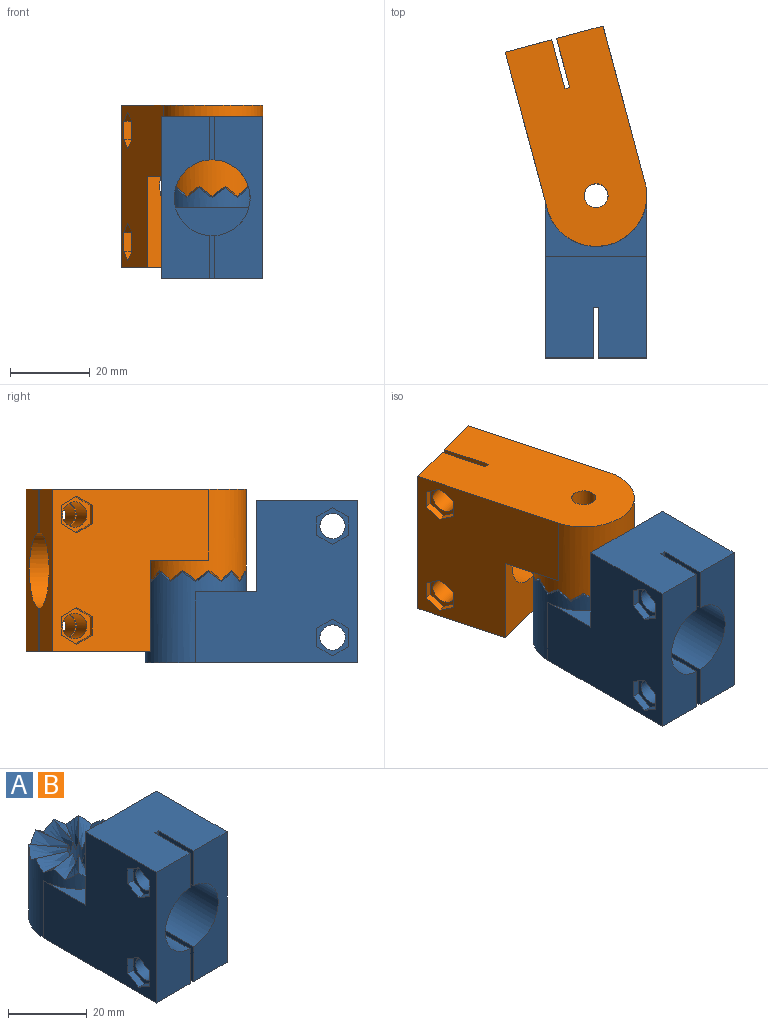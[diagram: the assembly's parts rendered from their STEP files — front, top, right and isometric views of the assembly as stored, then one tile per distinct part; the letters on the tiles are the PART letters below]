
ASSEMBLY  parts=2 mates=1
PART A: 62 faces, bbox 25.4x53.3x40.6 mm
  f0: plane 40.64x40.64mm, normal (-1,0,0), area 1192.4mm2, adj f3,f4,f5,f30,f31,f33,f49,f50
  f1: cylinder r=3.17mm len=10.07mm, axis (1,0,0), area 200.8mm2, adj f42,f55
  f2: cylinder r=3.17mm len=10.07mm, axis (1,0,0), area 200.8mm2, adj f39,f48
  f3: plane 40.64x12.07mm, normal (0,-1,0), area 359.9mm2, adj f0,f4,f31,f36,f39,f42
  f4: plane 25.4x25.4mm, normal (0,0,1), area 629mm2, adj f0,f3,f5,f32,f34,f41,f42,f43
  f5: plane 25.4x22.86mm, normal (0,1,0), area 390.3mm2, adj f0,f4,f32,f33,f36
  f6: bspline ~10.5x5.67mm, area 31.8mm2, adj f7,f29,f30,f35
  f7: bspline ~9.14x8.03mm, area 31.8mm2, adj f6,f8,f30,f35
  f8: bspline ~9.14x8.03mm, area 31.8mm2, adj f7,f9,f30,f35
  f9: bspline ~10.5x5.67mm, area 31.8mm2, adj f8,f10,f30,f35
  f10: bspline ~10.16x3.81mm, area 31.8mm2, adj f9,f11,f30,f35
  f11: bspline ~10.16x3.81mm, area 31.8mm2, adj f10,f12,f30,f35
  f12: bspline ~10.5x5.67mm, area 31.8mm2, adj f11,f13,f30,f35
  f13: bspline ~9.14x8.03mm, area 31.8mm2, adj f12,f14,f30,f35
  f14: bspline ~9.14x8.03mm, area 31.8mm2, adj f13,f15,f30,f35
  f15: bspline ~10.5x5.67mm, area 31.8mm2, adj f14,f16,f30,f35
  f16: bspline ~10.16x3.81mm, area 31.8mm2, adj f15,f17,f30,f35
  f17: bspline ~10.16x3.81mm, area 31.8mm2, adj f16,f18,f30,f35
  f18: bspline ~10.5x5.67mm, area 31.8mm2, adj f17,f19,f30,f35
  f19: bspline ~9.14x8.03mm, area 31.8mm2, adj f18,f20,f30,f35
  f20: bspline ~9.14x8.03mm, area 31.8mm2, adj f19,f21,f30,f35
  f21: bspline ~10.5x5.67mm, area 31.8mm2, adj f20,f22,f30,f35
  f22: bspline ~10.16x3.81mm, area 31.8mm2, adj f21,f23,f30,f35
  f23: bspline ~10.16x3.81mm, area 31.8mm2, adj f22,f24,f30,f35
  f24: bspline ~10.5x5.67mm, area 31.8mm2, adj f23,f25,f30,f35
  f25: bspline ~9.14x8.03mm, area 31.8mm2, adj f24,f26,f30,f35
  f26: bspline ~9.14x8.03mm, area 31.8mm2, adj f25,f27,f30,f35
  f27: bspline ~10.5x5.67mm, area 31.8mm2, adj f26,f28,f30,f35
  f28: bspline ~10.16x3.81mm, area 31.8mm2, adj f27,f29,f30,f35
  f29: bspline ~10.16x3.81mm, area 31.8mm2, adj f6,f28,f30,f35
  f30: cylinder r=12.7mm len=25.4mm, axis (0,0,-1), area 1011.1mm2, adj f0,f6,f7,f8,f9,f10,f11,f12
  f31: plane 53.34x25.4mm, normal (0,0,-1), area 1241.2mm2, adj f0,f3,f30,f32,f34,f35,f38,f39
  f32: plane 40.64x40.64mm, normal (1,0,0), area 1098mm2, adj f4,f5,f30,f31,f33,f34,f46,f47
  f33: plane 25.4x15.24mm, normal (0,0,1), area 133.7mm2, adj f0,f5,f30,f32,f37
  f34: plane 40.64x12.07mm, normal (0,-1,0), area 359.9mm2, adj f4,f31,f32,f36,f40,f41
  f35: cylinder r=3mm len=21.63mm, axis (0,0,-1), area 384mm2, adj f6,f7,f8,f9,f10,f11,f12,f13
  f36: cylinder r=9.53mm len=25.4mm, axis (0,-1,0), area 1487.8mm2, adj f3,f5,f34,f37,f38,f39,f40,f41
  f37: plane 18.36x6.99mm, normal (0,-1,0), area 94.7mm2, adj f33,f36
  f38: plane 10.82x1.27mm, normal (0,-1,0), area 13.7mm2, adj f31,f36,f39,f40
  f39: plane 12.7x10.82mm, normal (1,0,0), area 105.7mm2, adj f2,f3,f31,f36,f38
  f40: plane 12.7x10.82mm, normal (-1,0,0), area 105.7mm2, adj f31,f34,f36,f38,f45
  f41: plane 12.7x10.82mm, normal (-1,0,0), area 105.7mm2, adj f4,f34,f36,f43,f44
  f42: plane 12.7x10.82mm, normal (1,0,0), area 105.7mm2, adj f1,f3,f4,f36,f43
  f43: plane 10.82x1.27mm, normal (0,-1,0), area 13.7mm2, adj f4,f36,f41,f42
  f44: cylinder r=3.17mm len=9.53mm, axis (1,0,0), area 190mm2, adj f41,f47
  f45: cylinder r=3.17mm len=9.53mm, axis (1,0,0), area 190mm2, adj f40,f46
  f46: cone r=3.17mm half-angle=45deg, axis (1,0,0), area 100.3mm2, adj f32,f45
  f47: cone r=3.17mm half-angle=45deg, axis (1,0,0), area 100.3mm2, adj f32,f44
  f48: plane 9.24x8mm, normal (-1,0,0), area 23.8mm2, adj f2,f49,f50,f51,f52,f53,f54
  f49: plane 4x2.31mm, normal (0,0.5,-0.87), area 9.2mm2, adj f0,f48,f50,f54
  f50: plane 4x2.31mm, normal (0,-0.5,-0.87), area 9.2mm2, adj f0,f48,f49,f51
  f51: plane 4.62x2mm, normal (0,-1,0), area 9.2mm2, adj f0,f48,f50,f52
  f52: plane 4x2.31mm, normal (0,-0.5,0.87), area 9.2mm2, adj f0,f48,f51,f53
  f53: plane 4x2.31mm, normal (0,0.5,0.87), area 9.2mm2, adj f0,f48,f52,f54
  f54: plane 4.62x2mm, normal (0,1,0), area 9.2mm2, adj f0,f48,f49,f53
  f55: plane 9.24x8mm, normal (-1,0,0), area 23.8mm2, adj f1,f56,f57,f58,f59,f60,f61
  f56: plane 4x2.31mm, normal (0,0.5,-0.87), area 9.2mm2, adj f0,f55,f57,f61
  f57: plane 4x2.31mm, normal (0,-0.5,-0.87), area 9.2mm2, adj f0,f55,f56,f58
  f58: plane 4.62x2mm, normal (0,-1,0), area 9.2mm2, adj f0,f55,f57,f59
  f59: plane 4x2.31mm, normal (0,-0.5,0.87), area 9.2mm2, adj f0,f55,f58,f60
  f60: plane 4x2.31mm, normal (0,0.5,0.87), area 9.2mm2, adj f0,f55,f59,f61
  f61: plane 4.62x2mm, normal (0,1,0), area 9.2mm2, adj f0,f55,f56,f60
PART B: same geometry as A
PLACE A t=(3.62,0.48,34.8)mm
PLACE B rot(axis=(0.99,0.13,0),180deg) t=(3.62,0.48,42.77)mm
MATE revolute B.f30 <-> A.f30  axis (0,0,1) through (3.62,0.48,38.78)mm
